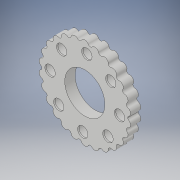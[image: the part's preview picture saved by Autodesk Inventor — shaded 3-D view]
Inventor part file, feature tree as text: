
AUTODESK INVENTOR PART (.ipt)
format: ipt  version: 2019.4 (Build 234330000, 330)  size: 391,680 bytes
history: native  units: mm
features: extrude x3, sketch x3, pattern_circular x1, other x1, projected_geometry x1
ambient origin geometry x8: Origin, YZ Plane, XZ Plane, XY Plane, X Axis, Y Axis, Z Axis, Center Point
bodies: Solid1 (feature_tree)
feature tree (9):
  extrude  "Extrusion1"  Depth=8.08mm
  extrude  "Extrusion3"  Depth=80.0mm TaperAngle=360.0deg
  pattern_circular  "Circular Pattern2"  [2 undecoded]
  extrude  "Extrusion4"  Depth=0.581776mm
  sketch  "Sketch1"  dims[d0=0.0mm d1=3600.0mm d2=8.08mm]
  other  "2D Equation Curve1"
  sketch  "Sketch3"  dims[d3=23.5mm d5=80.0mm d7=360.0deg]
  projected_geometry  "Projected Loop2"
  sketch  "Sketch5"  dims[d9=27.1mm d10=7.0mm d11=0.0mm d18=0.581776mm d19=7.0mm d20=1.0mm d21=0.0mm d22=80.0mm d23=360.0deg d28=1.0mm d29=0.0mm]
note: 2 required parameter values undecoded (feature->parameter linkage not recoverable at this tier; creation-order binding heuristic only, values carry confidence <= 0.55)
